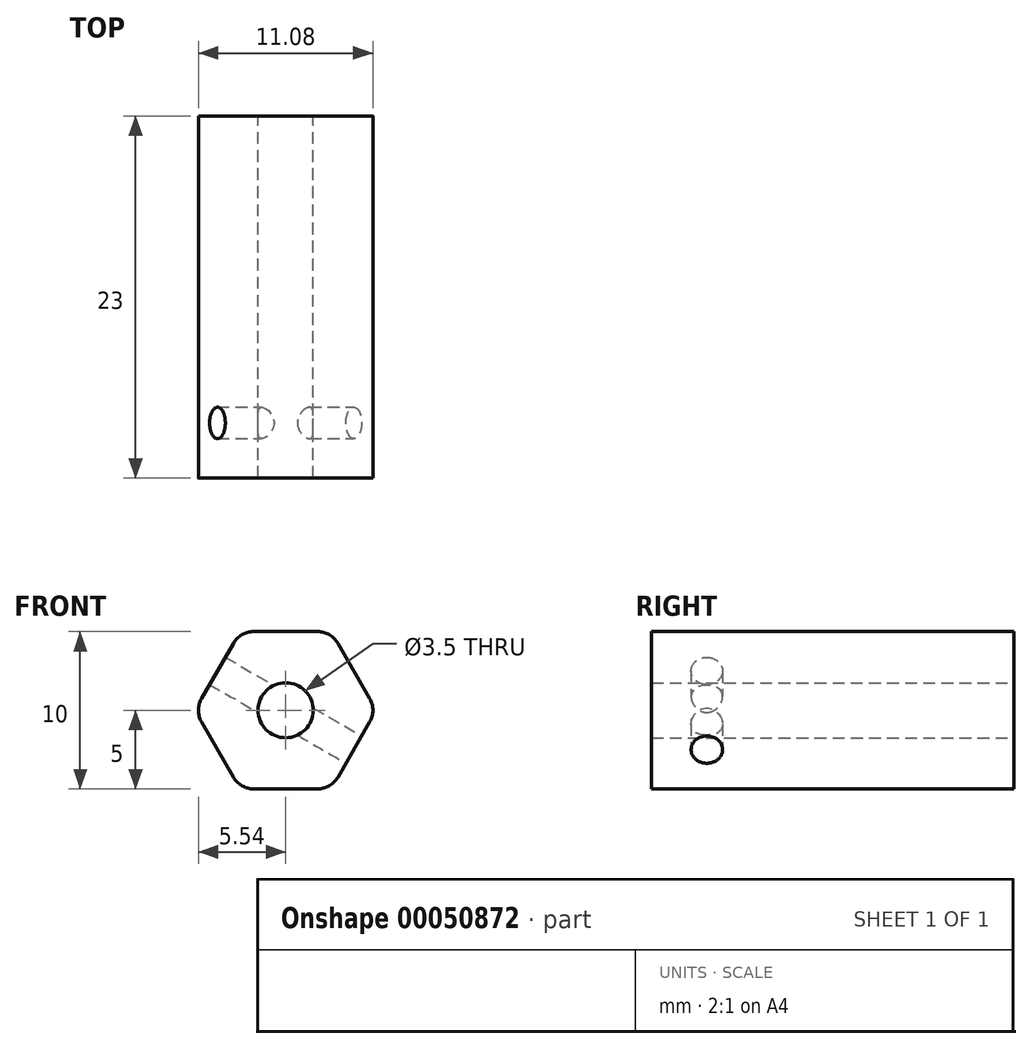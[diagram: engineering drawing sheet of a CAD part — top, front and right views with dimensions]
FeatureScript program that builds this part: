
annotation { "Feature Type Name" : "Feature", "Feature Type Description" : "" }
export const myFeature = defineFeature(function(context is Context, id is Id, definition is map)
    precondition{}
    {
        {
            var Q0;
            Q0=qCreatedBy(makeId("Front.planeOp"),FACE);
            var sketch = newSketch(context, id + "F0", { "sketchPlane" : qUnion([Q0])});
            skCircle(sketch, "E0.cCircle", {"center": v(0, 0) * mm, "radius": 5 * mm, "construction": true});
            skLineSegment(sketch, "E0.0", {"start": v(-5.77, 0) * mm, "end": v(-2.89, 5) * mm});
            skLineSegment(sketch, "E0.1", {"start": v(-2.89, 5) * mm, "end": v(2.89, 5) * mm});
            skLineSegment(sketch, "E0.2", {"start": v(2.89, 5) * mm, "end": v(5.77, 0) * mm});
            skLineSegment(sketch, "E0.3", {"start": v(5.77, 0) * mm, "end": v(2.89, -5) * mm});
            skLineSegment(sketch, "E0.4", {"start": v(2.89, -5) * mm, "end": v(-2.89, -5) * mm});
            skLineSegment(sketch, "E0.5", {"start": v(-2.89, -5) * mm, "end": v(-5.77, 0) * mm});
            skPoint(sketch, "E0.0.midPoint", {"position": v(-4.33, 2.5) * mm});
            skCircle(sketch, "E1", {"center": v(0, 0) * mm, "radius": 1.75 * mm});
            skSolve(sketch);
        }
        {
            var Q0;
            Q0=makeQuery(id+"F0.imprint","IMPRINT",FACE,{"disambiguationData":[TD([[makeQuery(id+"F0.imprint","IMPRINT",EDGE,{"derivedFrom":sQuery(id+"F0.wireOp",EDGE,"E0.0")}),-1.0]])]});
            extrude(context, id + "F1", {"entities" : qUnion([Q0]), "depth" : 23 * mm});
        }
        {
            var Q0;
            Q0=makeQuery(id+"F1.opExtrude","SWEPT_EDGE",EDGE,{"disambiguationData":[OSD([sQuery(id+"F0.wireOp",EDGE,"E0.1"),sQuery(id+"F0.wireOp",EDGE,"E0.2")])]});
            var Q1;
            Q1=makeQuery(id+"F1.opExtrude","SWEPT_EDGE",EDGE,{"disambiguationData":[OSD([sQuery(id+"F0.wireOp",EDGE,"E0.0"),sQuery(id+"F0.wireOp",EDGE,"E0.1")])]});
            var Q2;
            Q2=makeQuery(id+"F1.opExtrude","SWEPT_EDGE",EDGE,{"disambiguationData":[OSD([sQuery(id+"F0.wireOp",EDGE,"E0.2"),sQuery(id+"F0.wireOp",EDGE,"E0.3")])]});
            var Q3;
            Q3=makeQuery(id+"F1.opExtrude","SWEPT_EDGE",EDGE,{"disambiguationData":[OSD([sQuery(id+"F0.wireOp",EDGE,"E0.3"),sQuery(id+"F0.wireOp",EDGE,"E0.4")])]});
            var Q4;
            Q4=makeQuery(id+"F1.opExtrude","SWEPT_EDGE",EDGE,{"disambiguationData":[OSD([sQuery(id+"F0.wireOp",EDGE,"E0.4"),sQuery(id+"F0.wireOp",EDGE,"E0.5")])]});
            var Q5;
            Q5=makeQuery(id+"F1.opExtrude","SWEPT_EDGE",EDGE,{"disambiguationData":[OSD([sQuery(id+"F0.wireOp",EDGE,"E0.0"),sQuery(id+"F0.wireOp",EDGE,"E0.5")])]});
            fillet(context, id + "F2", {"entities" : qUnion([Q0, Q1, Q2, Q3, Q4, Q5]), "radius" : 1.5 * mm, "tangentPropagation" : true, "allowEdgeOverflow" : false});
        }
        {
            var Q0;
            Q0=makeQuery(id+"F1.opExtrude","SWEPT_FACE",FACE,{"disambiguationData":[OSD([sQuery(id+"F0.wireOp",EDGE,"E0.3")])]});
            var sketch = newSketch(context, id + "F3", { "sketchPlane" : qUnion([Q0])});
            skCircle(sketch, "E2", {"center": v(-19.5, 0) * mm, "radius": 1 * mm});
            skSolve(sketch);
        }
        {
            var Q0;
            Q0=makeQuery(id+"F3.imprint","IMPRINT",FACE,{"disambiguationData":[TD([[makeQuery(id+"F3.imprint","IMPRINT",EDGE,{"derivedFrom":sQuery(id+"F3.wireOp",EDGE,"E2")}),1.0]])]});
            var Q1;
            Q1=makeQuery(id+"F1.opExtrude","SWEPT_FACE",FACE,{"disambiguationData":[OSD([sQuery(id+"F0.wireOp",EDGE,"E0.0")])]});
            extrude(context, id + "F4", {"entities" : qUnion([Q0]), "operationType" : NewBodyOperationType.REMOVE, "endBound" : BoundingType.UP_TO_SURFACE, "oppositeDirection" : true, "endBoundEntityFace" : qUnion([Q1]), "depth" : 25 * mm});
        }
    });
